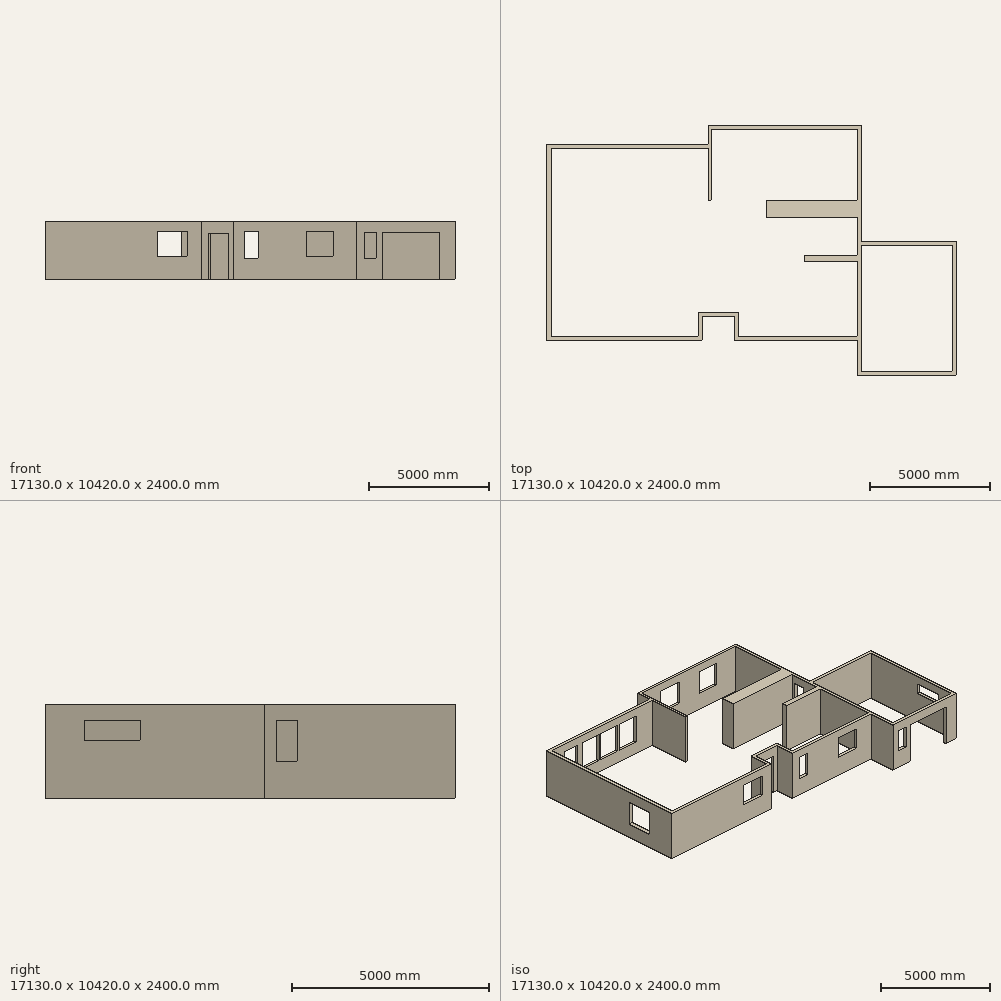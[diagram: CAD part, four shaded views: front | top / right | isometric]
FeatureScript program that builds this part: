
annotation { "Feature Type Name" : "Feature", "Feature Type Description" : "" }
export const myFeature = defineFeature(function(context is Context, id is Id, definition is map)
    precondition{}
    {
        {
            var Q0;
            Q0=qCreatedBy(makeId("Top.planeOp"),FACE);
            var sketch = newSketch(context, id + "F0", { "sketchPlane" : qUnion([Q0])});
            skLineSegment(sketch, "E0.bottom", {"start": v(160, 4090) * mm, "end": v(-6590, 4090) * mm});
            skLineSegment(sketch, "E0.top", {"start": v(6410, -4090) * mm, "end": v(1280, -4090) * mm});
            skLineSegment(sketch, "E0.right", {"start": v(-6590, 4090) * mm, "end": v(-6590, -4090) * mm});
            skPoint(sketch, "E0.middle", {"position": v(0, 0) * mm});
            skLineSegment(sketch, "E1.trimOffspring", {"start": v(-90, -4090) * mm, "end": v(-6590, -4090) * mm});
            skLineSegment(sketch, "E2", {"start": v(-90, -4090) * mm, "end": v(-90, -3090) * mm});
            skLineSegment(sketch, "E3", {"start": v(-90, -3090) * mm, "end": v(1280, -3090) * mm});
            skLineSegment(sketch, "E4", {"start": v(1280, -3090) * mm, "end": v(1280, -4090) * mm});
            skLineSegment(sketch, "E5", {"start": v(6410, -3925) * mm, "end": v(6410, -5530) * mm});
            skLineSegment(sketch, "E6", {"start": v(6575, -5365) * mm, "end": v(6575, -125) * mm});
            skLineSegment(sketch, "E7", {"start": v(6575, -125) * mm, "end": v(10375, -125) * mm});
            skLineSegment(sketch, "E8", {"start": v(10375, -125) * mm, "end": v(10375, -5365) * mm});
            skLineSegment(sketch, "E9", {"start": v(10375, -5530) * mm, "end": v(6575, -5530) * mm});
            skLineSegment(sketch, "E10", {"start": v(6410, -4090) * mm, "end": v(6410, -5530) * mm});
            skLineSegment(sketch, "E11", {"start": v(6410, -5530) * mm, "end": v(6575, -5530) * mm});
            skLineSegment(sketch, "E12", {"start": v(6560, 40) * mm, "end": v(10540, 40) * mm});
            skLineSegment(sketch, "E13", {"start": v(10540, 40) * mm, "end": v(10540, -5530) * mm});
            skLineSegment(sketch, "E14", {"start": v(10540, -5530) * mm, "end": v(10375, -5530) * mm});
            skLineSegment(sketch, "E15", {"start": v(6410, -5530) * mm, "end": v(6410, 4740) * mm});
            skLineSegment(sketch, "E16", {"start": v(-6375, 3940) * mm, "end": v(-6375, -3925) * mm});
            skLineSegment(sketch, "E17", {"start": v(-6375, -3925) * mm, "end": v(-255, -3925) * mm});
            skLineSegment(sketch, "E18", {"start": v(-255, -3925) * mm, "end": v(-255, -2925) * mm});
            skLineSegment(sketch, "E19", {"start": v(-255, -2925) * mm, "end": v(1445, -2925) * mm});
            skLineSegment(sketch, "E20", {"start": v(1445, -2925) * mm, "end": v(1445, -3925) * mm});
            skLineSegment(sketch, "E21", {"start": v(1445, -3925) * mm, "end": v(6410, -3925) * mm});
            skLineSegment(sketch, "E22", {"start": v(6575, -5365) * mm, "end": v(10375, -5365) * mm});
            skLineSegment(sketch, "E23.bottom", {"start": v(-255, -2925) * mm, "end": v(-105, -2925) * mm});
            skLineSegment(sketch, "E23.top", {"start": v(-255, -505) * mm, "end": v(-105, -505) * mm});
            skLineSegment(sketch, "E23.right", {"start": v(-105, -2925) * mm, "end": v(-105, -505) * mm});
            skLineSegment(sketch, "E24.bottom", {"start": v(-255, -505) * mm, "end": v(-2205, -505) * mm});
            skLineSegment(sketch, "E24.top", {"start": v(-255, -645) * mm, "end": v(-2865, -645) * mm});
            skLineSegment(sketch, "E25", {"start": v(-255, -645) * mm, "end": v(-255, -2925) * mm});
            skLineSegment(sketch, "E26", {"start": v(160, 4090) * mm, "end": v(160, 4890) * mm});
            skLineSegment(sketch, "E27", {"start": v(160, 4890) * mm, "end": v(6560, 4890) * mm});
            skLineSegment(sketch, "E28", {"start": v(6560, 4890) * mm, "end": v(6560, 40) * mm});
            skLineSegment(sketch, "E29", {"start": v(310, 4740) * mm, "end": v(6410, 4740) * mm});
            skLineSegment(sketch, "E30", {"start": v(310, 4740) * mm, "end": v(310, 3940) * mm});
            skLineSegment(sketch, "E31", {"start": v(310, 3940) * mm, "end": v(-6375, 3940) * mm});
            skLineSegment(sketch, "E32", {"start": v(175, 3940) * mm, "end": v(175, 1760) * mm});
            skLineSegment(sketch, "E33", {"start": v(175, 1760) * mm, "end": v(310, 1760) * mm});
            skLineSegment(sketch, "E34", {"start": v(310, 1760) * mm, "end": v(310, 3940) * mm});
            skLineSegment(sketch, "E35.bottom", {"start": v(6410, 1760) * mm, "end": v(2590, 1760) * mm});
            skLineSegment(sketch, "E35.top", {"start": v(6410, 1055) * mm, "end": v(2590, 1055) * mm});
            skLineSegment(sketch, "E35.left", {"start": v(6410, 1760) * mm, "end": v(6410, 1055) * mm});
            skLineSegment(sketch, "E35.right", {"start": v(2590, 1760) * mm, "end": v(2590, 1055) * mm});
            skLineSegment(sketch, "E36.bottom", {"start": v(6410, -785) * mm, "end": v(4210, -785) * mm});
            skLineSegment(sketch, "E36.top", {"start": v(6410, -535) * mm, "end": v(4210, -535) * mm});
            skLineSegment(sketch, "E36.left", {"start": v(6410, -785) * mm, "end": v(6410, -535) * mm});
            skLineSegment(sketch, "E36.right", {"start": v(4210, -785) * mm, "end": v(4210, -535) * mm});
            skLineSegment(sketch, "E37.bottom", {"start": v(3485, -3925) * mm, "end": v(3560, -3925) * mm});
            skLineSegment(sketch, "E37.left", {"start": v(3560, -3925) * mm, "end": v(3560, -1725) * mm});
            skLineSegment(sketch, "E37.right", {"start": v(3485, -3925) * mm, "end": v(3485, -1825) * mm});
            skLineSegment(sketch, "E38.bottom", {"start": v(1445, -2925) * mm, "end": v(1265, -2925) * mm});
            skLineSegment(sketch, "E38.left", {"start": v(1445, -2925) * mm, "end": v(1445, -555) * mm});
            skLineSegment(sketch, "E38.right", {"start": v(1265, -2925) * mm, "end": v(1265, -555) * mm});
            skLineSegment(sketch, "E39.bottom", {"start": v(1445, -555) * mm, "end": v(1760.37, -555) * mm});
            skLineSegment(sketch, "E39.top", {"start": v(1265, -455) * mm, "end": v(1760.37, -455) * mm});
            skLineSegment(sketch, "E39.right", {"start": v(1760.37, -555) * mm, "end": v(1760.37, -455) * mm});
            skLineSegment(sketch, "E40", {"start": v(1265, -555) * mm, "end": v(1265, -455) * mm});
            skLineSegment(sketch, "E41", {"start": v(2601.43, -555) * mm, "end": v(3025, -555) * mm});
            skLineSegment(sketch, "E42", {"start": v(3025, -555) * mm, "end": v(3025, -1825) * mm});
            skLineSegment(sketch, "E43", {"start": v(3025, -1825) * mm, "end": v(3485, -1825) * mm});
            skLineSegment(sketch, "E44", {"start": v(2601.43, -555) * mm, "end": v(2601.43, -455) * mm});
            skLineSegment(sketch, "E45", {"start": v(2601.43, -455) * mm, "end": v(3125, -455) * mm});
            skLineSegment(sketch, "E46", {"start": v(3125, -455) * mm, "end": v(3125, -1725) * mm});
            skLineSegment(sketch, "E47", {"start": v(3125, -1725) * mm, "end": v(3560, -1725) * mm});
            skLineSegment(sketch, "E48", {"start": v(-2205, -505) * mm, "end": v(-2205, -395) * mm});
            skLineSegment(sketch, "E49", {"start": v(-2205, -395) * mm, "end": v(-3495, -395) * mm});
            skLineSegment(sketch, "E50", {"start": v(-3495, -395) * mm, "end": v(-3495, -1265) * mm});
            skLineSegment(sketch, "E51", {"start": v(-3495, -1265) * mm, "end": v(-2865, -1265) * mm});
            skLineSegment(sketch, "E52", {"start": v(-2865, -1265) * mm, "end": v(-2865, -645) * mm});
            skSolve(sketch);
        }
        {
            var Q0;
            Q0=makeQuery(id+"F0.imprint","IMPRINT",FACE,{"disambiguationData":[TD([[makeQuery(id+"F0.imprint","IMPRINT",EDGE,{"derivedFrom":sQuery(id+"F0.wireOp",EDGE,"E35.bottom")}),1.0]])]});
            var Q1;
            Q1=makeQuery(id+"F0.imprint","IMPRINT",FACE,{"disambiguationData":[TD([[makeQuery(id+"F0.imprint","IMPRINT",EDGE,{"derivedFrom":sQuery(id+"F0.wireOp",EDGE,"E0.bottom")}),1.0]])]});
            var Q2;
            Q2=makeQuery(id+"F0.imprint","IMPRINT",FACE,{"disambiguationData":[TD([[makeQuery(id+"F0.imprint","IMPRINT",EDGE,{"derivedFrom":sQuery(id+"F0.wireOp",EDGE,"E36.bottom")}),-1.0]])]});
            var Q3;
            Q3=makeQuery(id+"F0.imprint","IMPRINT",FACE,{"disambiguationData":[TD([[makeQuery(id+"F0.imprint","IMPRINT",EDGE,{"derivedFrom":sQuery(id+"F0.wireOp",EDGE,"E37.bottom")}),1.0]])]});
            var Q4;
            Q4=makeQuery(id+"F0.imprint","IMPRINT",FACE,{"disambiguationData":[TD([[makeQuery(id+"F0.imprint","IMPRINT",EDGE,{"derivedFrom":sQuery(id+"F0.wireOp",EDGE,"E38.bottom")}),-1.0]])]});
            var Q5;
            Q5=makeQuery(id+"F0.imprint","IMPRINT",FACE,{"disambiguationData":[TD([[makeQuery(id+"F0.imprint","IMPRINT",EDGE,{"derivedFrom":sQuery(id+"F0.wireOp",EDGE,"E23.bottom")}),1.0]])]});
            var Q6;
            {var subQ2=sQuery(id+"F0.wireOp",EDGE,"E32");Q6=makeQuery(id+"F0.imprint","IMPRINT",FACE,{"disambiguationData":[TD([[makeQuery(id+"F0.imprint","IMPRINT",EDGE,{"derivedFrom":subQ2}),1.0]])]});}
            extrude(context, id + "F1", {"entities" : qUnion([Q0, Q1, Q2, Q3, Q4, Q5, Q6]), "depth" : 2400 * mm, "offsetDistance" : 25 * mm});
        }
        {
            var Q0;
            Q0=makeQuery(id+"F1.opExtrude","SWEPT_FACE",FACE,{"disambiguationData":[OSD([sQuery(id+"F0.wireOp",EDGE,"E1.trimOffspring")])]});
            var sketch = newSketch(context, id + "F2", { "sketchPlane" : qUnion([Q0])});
            skLineSegment(sketch, "E53.bottom", {"start": v(-1910, 2000) * mm, "end": v(-650, 2000) * mm});
            skLineSegment(sketch, "E53.top", {"start": v(-1910, 960) * mm, "end": v(-650, 960) * mm});
            skLineSegment(sketch, "E53.left", {"start": v(-1910, 2000) * mm, "end": v(-1910, 960) * mm});
            skLineSegment(sketch, "E53.right", {"start": v(-650, 2000) * mm, "end": v(-650, 960) * mm});
            skLineSegment(sketch, "E54.bottom", {"start": v(1740, 2000) * mm, "end": v(2290, 2000) * mm});
            skLineSegment(sketch, "E54.top", {"start": v(1740, 850) * mm, "end": v(2290, 850) * mm});
            skLineSegment(sketch, "E54.left", {"start": v(1740, 2000) * mm, "end": v(1740, 850) * mm});
            skLineSegment(sketch, "E54.right", {"start": v(2290, 2000) * mm, "end": v(2290, 850) * mm});
            skLineSegment(sketch, "E55.bottom", {"start": v(4310, 2000) * mm, "end": v(5460, 2000) * mm});
            skLineSegment(sketch, "E55.top", {"start": v(4310, 950) * mm, "end": v(5460, 950) * mm});
            skLineSegment(sketch, "E55.left", {"start": v(4310, 2000) * mm, "end": v(4310, 950) * mm});
            skLineSegment(sketch, "E55.right", {"start": v(5460, 2000) * mm, "end": v(5460, 950) * mm});
            skSolve(sketch);
        }
        {
            var Q0;
            Q0=makeQuery(id+"F2.imprint","IMPRINT",FACE,{"disambiguationData":[TD([[makeQuery(id+"F2.imprint","IMPRINT",EDGE,{"derivedFrom":sQuery(id+"F2.wireOp",EDGE,"E53.bottom")}),-1.0]])]});
            var Q1;
            Q1=makeQuery(id+"F2.imprint","IMPRINT",FACE,{"disambiguationData":[TD([[makeQuery(id+"F2.imprint","IMPRINT",EDGE,{"derivedFrom":sQuery(id+"F2.wireOp",EDGE,"E54.bottom")}),-1.0]])]});
            var Q2;
            Q2=makeQuery(id+"F2.imprint","IMPRINT",FACE,{"disambiguationData":[TD([[makeQuery(id+"F2.imprint","IMPRINT",EDGE,{"derivedFrom":sQuery(id+"F2.wireOp",EDGE,"E55.bottom")}),-1.0]])]});
            extrude(context, id + "F3", {"entities" : qUnion([Q0, Q1, Q2]), "operationType" : NewBodyOperationType.REMOVE, "endBound" : BoundingType.UP_TO_NEXT, "oppositeDirection" : true, "depth" : 25 * mm, "offsetDistance" : 25 * mm});
        }
        {
            var Q0;
            Q0=makeQuery(id+"F1.opExtrude","SWEPT_FACE",FACE,{"disambiguationData":[OSD([sQuery(id+"F0.wireOp",EDGE,"E0.right")])]});
            var sketch = newSketch(context, id + "F4", { "sketchPlane" : qUnion([Q0])});
            skLineSegment(sketch, "E56.bottom", {"start": v(1313.87, 1862.42) * mm, "end": v(2633.87, 1862.42) * mm});
            skLineSegment(sketch, "E56.top", {"start": v(1313.87, 712.42) * mm, "end": v(2633.87, 712.42) * mm});
            skLineSegment(sketch, "E56.left", {"start": v(1313.87, 1862.42) * mm, "end": v(1313.87, 712.42) * mm});
            skLineSegment(sketch, "E56.right", {"start": v(2633.87, 1862.42) * mm, "end": v(2633.87, 712.42) * mm});
            skSolve(sketch);
        }
        {
            var Q0;
            Q0 = qSketchRegion(id + "F4", true);
            extrude(context, id + "F5", {"entities" : qUnion([Q0]), "operationType" : NewBodyOperationType.REMOVE, "endBound" : BoundingType.UP_TO_NEXT, "oppositeDirection" : true, "depth" : 25 * mm, "offsetDistance" : 25 * mm});
        }
        {
            var Q0;
            Q0=makeQuery(id+"F1.opExtrude","SWEPT_FACE",FACE,{"disambiguationData":[OSD([sQuery(id+"F0.wireOp",EDGE,"E0.bottom")])]});
            var sketch = newSketch(context, id + "F6", { "sketchPlane" : qUnion([Q0])});
            skLineSegment(sketch, "E57.bottom", {"start": v(4730, 2000) * mm, "end": v(5580, 2000) * mm});
            skLineSegment(sketch, "E57.top", {"start": v(4730, 0) * mm, "end": v(5580, 0) * mm});
            skLineSegment(sketch, "E57.left", {"start": v(4730, 2000) * mm, "end": v(4730, 0) * mm});
            skLineSegment(sketch, "E57.right", {"start": v(5580, 2000) * mm, "end": v(5580, 0) * mm});
            skPoint(sketch, "E58.firstSnap0", {"position": v(5155, 2000) * mm});
            skLineSegment(sketch, "E58.bottom", {"start": v(4400, 2000) * mm, "end": v(3300, 2000) * mm});
            skLineSegment(sketch, "E58.top", {"start": v(4400, 600) * mm, "end": v(3300, 600) * mm});
            skLineSegment(sketch, "E58.left", {"start": v(4400, 2000) * mm, "end": v(4400, 600) * mm});
            skLineSegment(sketch, "E58.right", {"start": v(3300, 2000) * mm, "end": v(3300, 600) * mm});
            skLineSegment(sketch, "E59.bottom", {"start": v(3200, 2000) * mm, "end": v(2100, 2000) * mm});
            skLineSegment(sketch, "E59.top", {"start": v(3200, 600) * mm, "end": v(2100, 600) * mm});
            skLineSegment(sketch, "E59.left", {"start": v(3200, 2000) * mm, "end": v(3200, 600) * mm});
            skLineSegment(sketch, "E59.right", {"start": v(2100, 2000) * mm, "end": v(2100, 600) * mm});
            skLineSegment(sketch, "E60.bottom", {"start": v(2000, 2000) * mm, "end": v(900, 2000) * mm});
            skLineSegment(sketch, "E60.top", {"start": v(2000, 600) * mm, "end": v(900, 600) * mm});
            skLineSegment(sketch, "E60.left", {"start": v(2000, 2000) * mm, "end": v(2000, 600) * mm});
            skLineSegment(sketch, "E60.right", {"start": v(900, 2000) * mm, "end": v(900, 600) * mm});
            skSolve(sketch);
        }
        {
            var Q0;
            Q0 = qSketchRegion(id + "F6", true);
            extrude(context, id + "F7", {"entities" : qUnion([Q0]), "operationType" : NewBodyOperationType.REMOVE, "endBound" : BoundingType.UP_TO_NEXT, "oppositeDirection" : true, "depth" : 25 * mm, "offsetDistance" : 25 * mm});
        }
        {
            var Q0;
            Q0=makeQuery(id+"F1.opExtrude","SWEPT_FACE",FACE,{"disambiguationData":[OSD([sQuery(id+"F0.wireOp",EDGE,"E27")])]});
            var sketch = newSketch(context, id + "F8", { "sketchPlane" : qUnion([Q0])});
            skLineSegment(sketch, "E61.bottom", {"start": v(-5160, 2000) * mm, "end": v(-4010, 2000) * mm});
            skLineSegment(sketch, "E61.top", {"start": v(-5160, 850) * mm, "end": v(-4010, 850) * mm});
            skLineSegment(sketch, "E61.left", {"start": v(-5160, 2000) * mm, "end": v(-5160, 850) * mm});
            skLineSegment(sketch, "E61.right", {"start": v(-4010, 2000) * mm, "end": v(-4010, 850) * mm});
            skLineSegment(sketch, "E62.bottom", {"start": v(-2760, 2000) * mm, "end": v(-1510, 2000) * mm});
            skLineSegment(sketch, "E62.top", {"start": v(-2760, 850) * mm, "end": v(-1510, 850) * mm});
            skLineSegment(sketch, "E62.left", {"start": v(-2760, 2000) * mm, "end": v(-2760, 850) * mm});
            skLineSegment(sketch, "E62.right", {"start": v(-1510, 2000) * mm, "end": v(-1510, 850) * mm});
            skSolve(sketch);
        }
        {
            var Q0;
            Q0 = qSketchRegion(id + "F8", true);
            extrude(context, id + "F9", {"entities" : qUnion([Q0]), "operationType" : NewBodyOperationType.REMOVE, "endBound" : BoundingType.UP_TO_NEXT, "oppositeDirection" : true, "depth" : 25 * mm, "offsetDistance" : 25 * mm});
        }
        {
            var Q0;
            Q0=makeQuery(id+"F1.opExtrude","SWEPT_FACE",FACE,{"disambiguationData":[OSD([sQuery(id+"F0.wireOp",EDGE,"E28")])]});
            var sketch = newSketch(context, id + "F10", { "sketchPlane" : qUnion([Q0])});
            skLineSegment(sketch, "E63.bottom", {"start": v(340, 2000) * mm, "end": v(880, 2000) * mm});
            skLineSegment(sketch, "E63.top", {"start": v(340, 940) * mm, "end": v(880, 940) * mm});
            skLineSegment(sketch, "E63.left", {"start": v(340, 2000) * mm, "end": v(340, 940) * mm});
            skLineSegment(sketch, "E63.right", {"start": v(880, 2000) * mm, "end": v(880, 940) * mm});
            skSolve(sketch);
        }
        {
            var Q0;
            Q0 = qSketchRegion(id + "F10", true);
            extrude(context, id + "F11", {"entities" : qUnion([Q0]), "operationType" : NewBodyOperationType.REMOVE, "endBound" : BoundingType.UP_TO_NEXT, "oppositeDirection" : true, "depth" : 25 * mm, "offsetDistance" : 25 * mm});
        }
        {
            var Q0;
            Q0=makeQuery(id+"F1.opExtrude","SWEPT_FACE",FACE,{"disambiguationData":[OSD([sQuery(id+"F0.wireOp",EDGE,"E13")])]});
            var sketch = newSketch(context, id + "F12", { "sketchPlane" : qUnion([Q0])});
            skLineSegment(sketch, "E64.bottom", {"start": v(-4542.74, 2000) * mm, "end": v(-3122.74, 2000) * mm});
            skLineSegment(sketch, "E64.top", {"start": v(-4542.74, 1490) * mm, "end": v(-3122.74, 1490) * mm});
            skLineSegment(sketch, "E64.left", {"start": v(-4542.74, 2000) * mm, "end": v(-4542.74, 1490) * mm});
            skLineSegment(sketch, "E64.right", {"start": v(-3122.74, 2000) * mm, "end": v(-3122.74, 1490) * mm});
            skSolve(sketch);
        }
        {
            var Q0;
            Q0 = qSketchRegion(id + "F12", true);
            extrude(context, id + "F13", {"entities" : qUnion([Q0]), "operationType" : NewBodyOperationType.REMOVE, "endBound" : BoundingType.UP_TO_NEXT, "oppositeDirection" : true, "depth" : 25 * mm, "offsetDistance" : 25 * mm});
        }
        {
            var Q0;
            Q0=makeQuery(id+"F1.opExtrude","SWEPT_FACE",FACE,{"disambiguationData":[OSD([sQuery(id+"F0.wireOp",EDGE,"E9"),sQuery(id+"F0.wireOp",EDGE,"E11"),sQuery(id+"F0.wireOp",EDGE,"E14")])]});
            var sketch = newSketch(context, id + "F14", { "sketchPlane" : qUnion([Q0])});
            skLineSegment(sketch, "E65.bottom", {"start": v(7510, 0) * mm, "end": v(9860, 0) * mm});
            skLineSegment(sketch, "E65.top", {"start": v(7510, 1960) * mm, "end": v(9860, 1960) * mm});
            skLineSegment(sketch, "E65.left", {"start": v(7510, 0) * mm, "end": v(7510, 1960) * mm});
            skLineSegment(sketch, "E65.right", {"start": v(9860, 0) * mm, "end": v(9860, 1960) * mm});
            skLineSegment(sketch, "E66.bottom", {"start": v(6740.25, 1960) * mm, "end": v(7260.25, 1960) * mm});
            skLineSegment(sketch, "E66.top", {"start": v(6740.25, 883) * mm, "end": v(7260.25, 883) * mm});
            skLineSegment(sketch, "E66.left", {"start": v(6740.25, 1960) * mm, "end": v(6740.25, 883) * mm});
            skLineSegment(sketch, "E66.right", {"start": v(7260.25, 1960) * mm, "end": v(7260.25, 883) * mm});
            skSolve(sketch);
        }
        {
            var Q0;
            Q0 = qSketchRegion(id + "F14", true);
            extrude(context, id + "F15", {"entities" : qUnion([Q0]), "operationType" : NewBodyOperationType.REMOVE, "endBound" : BoundingType.UP_TO_NEXT, "oppositeDirection" : true, "depth" : 25 * mm, "offsetDistance" : 25 * mm});
        }
        {
            var Q0;
            Q0=makeQuery(id+"F1.opExtrude","SWEPT_FACE",FACE,{"disambiguationData":[OSD([sQuery(id+"F0.wireOp",EDGE,"E3")])]});
            var sketch = newSketch(context, id + "F16", { "sketchPlane" : qUnion([Q0])});
            skLineSegment(sketch, "E67.bottom", {"start": v(212.86, 1930) * mm, "end": v(1052.86, 1930) * mm});
            skLineSegment(sketch, "E67.top", {"start": v(212.86, 0) * mm, "end": v(1052.86, 0) * mm});
            skLineSegment(sketch, "E67.left", {"start": v(212.86, 1930) * mm, "end": v(212.86, 0) * mm});
            skLineSegment(sketch, "E67.right", {"start": v(1052.86, 1930) * mm, "end": v(1052.86, 0) * mm});
            skSolve(sketch);
        }
        {
            var Q0;
            Q0 = qSketchRegion(id + "F16", true);
            extrude(context, id + "F17", {"entities" : qUnion([Q0]), "operationType" : NewBodyOperationType.REMOVE, "endBound" : BoundingType.UP_TO_NEXT, "oppositeDirection" : true, "depth" : 25 * mm, "offsetDistance" : 25 * mm});
        }
    });
